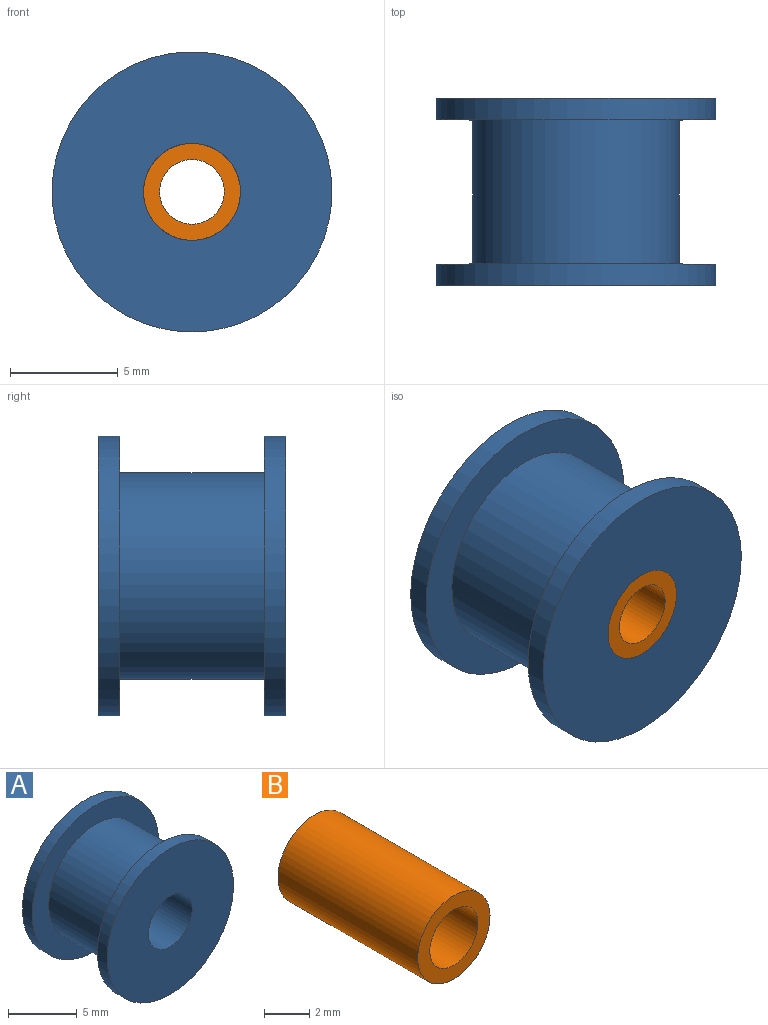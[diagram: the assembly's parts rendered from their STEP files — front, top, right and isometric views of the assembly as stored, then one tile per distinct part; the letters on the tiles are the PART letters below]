
ASSEMBLY  parts=2 mates=1
PART A: 8 faces, bbox 13x8.7x13 mm
  f0: cylinder r=6.5mm len=13mm, axis (0,-1,0), area 40.8mm2, adj f1,f7
  f1: plane 13x13mm, normal (0,-1,0), area 116.8mm2, adj f0,f2
  f2: cylinder r=2.25mm len=8.7mm, axis (0,-1,0), area 123mm2, adj f1,f3
  f3: plane 13x13mm, normal (0,1,0), area 116.8mm2, adj f2,f4
  f4: cylinder r=6.5mm len=13mm, axis (0,-1,0), area 40.8mm2, adj f3,f5
  f5: plane 13x13mm, normal (0,-1,0), area 60.3mm2, adj f4,f6
  f6: cylinder r=4.8mm len=9.6mm, axis (0,-1,0), area 202.1mm2, adj f5,f7
  f7: plane 13x13mm, normal (0,1,0), area 60.3mm2, adj f0,f6
PART B: 4 faces, bbox 4.5x8.7x4.5 mm
  f0: cylinder r=1.5mm len=8.7mm, axis (0,-1,0), area 82mm2, adj f1,f3
  f1: plane 4.5x4.5mm, normal (0,1,0), area 8.8mm2, adj f0,f2
  f2: cylinder r=2.25mm len=8.7mm, axis (0,-1,0), area 123mm2, adj f1,f3
  f3: plane 4.5x4.5mm, normal (0,-1,0), area 8.8mm2, adj f0,f2
PLACE A t=(0,-4.35,0)mm
PLACE B rot(axis=(0,1,0),47.1deg) t=(0,-4.35,0)mm
MATE revolute B.f0 <-> A.f0  axis (0,-1,0) through (0,-8.7,0)mm
